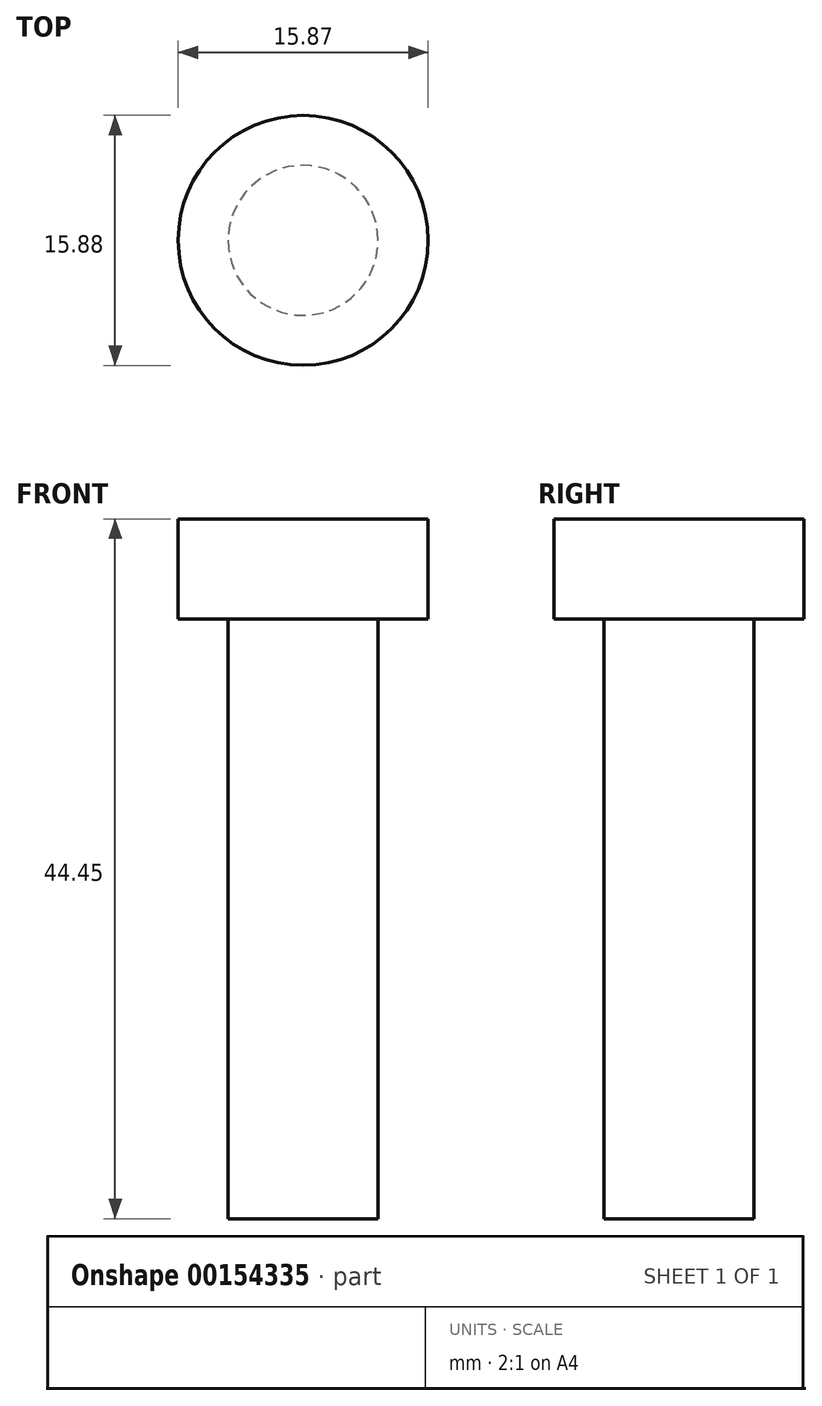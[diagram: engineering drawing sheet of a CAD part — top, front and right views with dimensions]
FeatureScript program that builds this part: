
annotation { "Feature Type Name" : "Feature", "Feature Type Description" : "" }
export const myFeature = defineFeature(function(context is Context, id is Id, definition is map)
    precondition{}
    {
        {
            var Q0;
            Q0=qCreatedBy(makeId("Front.planeOp"),FACE);
            var sketch = newSketch(context, id + "F0", { "sketchPlane" : qUnion([Q0])});
            skLineSegment(sketch, "E0", {"start": v(13.13, -48.85) * mm, "end": v(13.13, -10.75) * mm});
            skLineSegment(sketch, "E1", {"start": v(13.13, -10.75) * mm, "end": v(13.13, -4.4) * mm});
            skLineSegment(sketch, "E2.bottom", {"start": v(13.13, -48.85) * mm, "end": v(17.89, -48.85) * mm});
            skLineSegment(sketch, "E2.top", {"start": v(13.13, -10.75) * mm, "end": v(17.89, -10.75) * mm});
            skLineSegment(sketch, "E2.right", {"start": v(17.89, -48.85) * mm, "end": v(17.89, -10.75) * mm});
            skLineSegment(sketch, "E3.bottom", {"start": v(13.13, -10.75) * mm, "end": v(21.06, -10.75) * mm});
            skLineSegment(sketch, "E3.top", {"start": v(13.13, -4.4) * mm, "end": v(21.06, -4.4) * mm});
            skLineSegment(sketch, "E3.right", {"start": v(21.06, -10.75) * mm, "end": v(21.06, -4.4) * mm});
            skSolve(sketch);
        }
        {
            var Q0;
            Q0=makeQuery(id+"F0.imprint","IMPRINT",FACE,{"disambiguationData":[TD([[makeQuery(id+"F0.imprint","IMPRINT",EDGE,{"derivedFrom":sQuery(id+"F0.wireOp",EDGE,"E2.bottom")}),1.0]])]});
            var Q1;
            Q1=sQuery(id+"F0.wireOp",EDGE,"E0");
            revolve(context, id + "F1", {"entities" : qUnion([Q0]), "axis" : qUnion([Q1]), "revolveType" : RevolveType.FULL});
        }
        {
            var Q0;
            Q0=makeQuery(id+"F0.imprint","IMPRINT",FACE,{"disambiguationData":[TD([[makeQuery(id+"F0.imprint","IMPRINT",EDGE,{"derivedFrom":sQuery(id+"F0.wireOp",EDGE,"E3.top")}),-1.0]])]});
            var Q1;
            Q1=sQuery(id+"F0.wireOp",EDGE,"E1");
            revolve(context, id + "F2", {"operationType" : NewBodyOperationType.ADD, "entities" : qUnion([Q0]), "axis" : qUnion([Q1]), "revolveType" : RevolveType.FULL});
        }
    });
